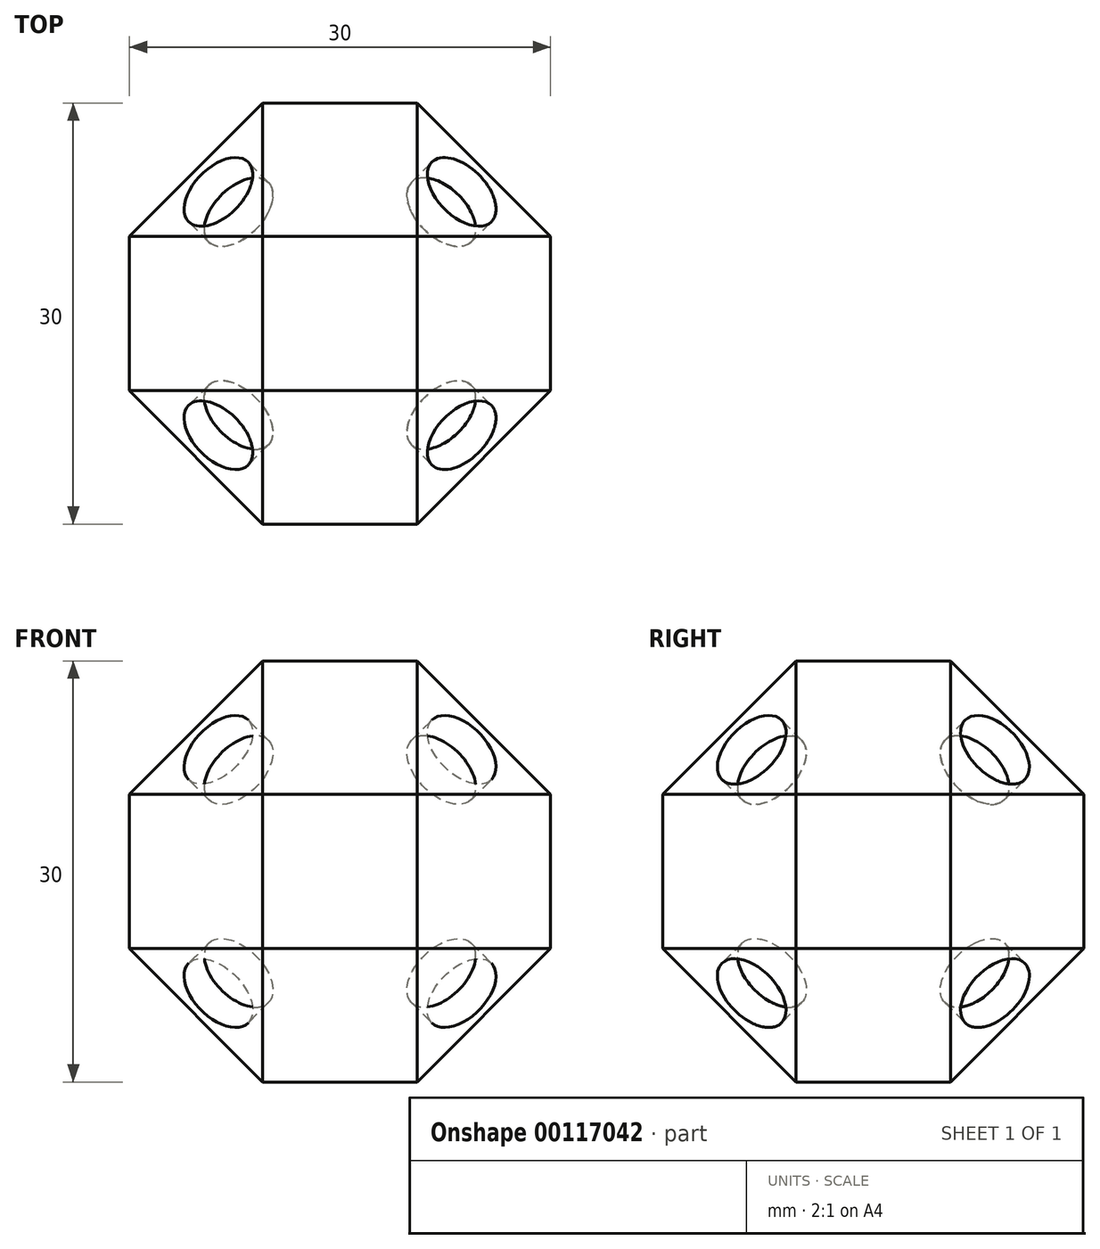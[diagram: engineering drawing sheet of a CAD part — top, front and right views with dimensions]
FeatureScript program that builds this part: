
annotation { "Feature Type Name" : "Feature", "Feature Type Description" : "" }
export const myFeature = defineFeature(function(context is Context, id is Id, definition is map)
    precondition{}
    {
        {
            var Q0;
            Q0=qCreatedBy(makeId("Front.planeOp"),FACE);
            var sketch = newSketch(context, id + "F0", { "sketchPlane" : qUnion([Q0])});
            skLineSegment(sketch, "E0.bottom", {"start": v(15, -15) * mm, "end": v(-15, -15) * mm});
            skLineSegment(sketch, "E0.top", {"start": v(15, 15) * mm, "end": v(-15, 15) * mm});
            skLineSegment(sketch, "E0.left", {"start": v(15, -15) * mm, "end": v(15, 15) * mm});
            skLineSegment(sketch, "E0.right", {"start": v(-15, -15) * mm, "end": v(-15, 15) * mm});
            skPoint(sketch, "E0.middle", {"position": v(0, 0) * mm});
            skLineSegment(sketch, "E1", {"start": v(15, 6.02) * mm, "end": v(6.02, 15) * mm, "construction": true});
            skLineSegment(sketch, "E2", {"start": v(15, 15) * mm, "end": v(10.5, 10.5) * mm, "construction": true});
            skSolve(sketch);
        }
        {
            var Q0;
            Q0 = qSketchRegion(id + "F0", true);
            extrude(context, id + "F1", {"entities" : qUnion([Q0]), "endBound" : BoundingType.SYMMETRIC, "depth" : 30 * mm});
        }
        {
            var Q0;
            Q0=makeQuery(id+"F1.opExtrude","CAP_EDGE",EDGE,{"disambiguationData":[OSD([sQuery(id+"F0.wireOp",EDGE,"E0.bottom")])],"isStart":true});
            var Q1;
            Q1=makeQuery(id+"F1.opExtrude","CAP_EDGE",EDGE,{"disambiguationData":[OSD([sQuery(id+"F0.wireOp",EDGE,"E0.top")])],"isStart":true});
            var Q2;
            Q2=makeQuery(id+"F1.opExtrude","CAP_EDGE",EDGE,{"disambiguationData":[OSD([sQuery(id+"F0.wireOp",EDGE,"E0.left")])],"isStart":true});
            var Q3;
            Q3=makeQuery(id+"F1.opExtrude","CAP_EDGE",EDGE,{"disambiguationData":[OSD([sQuery(id+"F0.wireOp",EDGE,"E0.right")])],"isStart":true});
            var Q4;
            Q4=makeQuery(id+"F1.opExtrude","SWEPT_EDGE",EDGE,{"disambiguationData":[OSD([sQuery(id+"F0.wireOp",EDGE,"E0.top"),sQuery(id+"F0.wireOp",EDGE,"E0.left")])]});
            var Q5;
            Q5=makeQuery(id+"F1.opExtrude","CAP_EDGE",EDGE,{"disambiguationData":[OSD([sQuery(id+"F0.wireOp",EDGE,"E0.top")])],"isStart":false});
            var Q6;
            Q6=makeQuery(id+"F1.opExtrude","SWEPT_EDGE",EDGE,{"disambiguationData":[OSD([sQuery(id+"F0.wireOp",EDGE,"E0.top"),sQuery(id+"F0.wireOp",EDGE,"E0.right")])]});
            var Q7;
            Q7=makeQuery(id+"F1.opExtrude","CAP_EDGE",EDGE,{"disambiguationData":[OSD([sQuery(id+"F0.wireOp",EDGE,"E0.right")])],"isStart":false});
            var Q8;
            Q8=makeQuery(id+"F1.opExtrude","CAP_EDGE",EDGE,{"disambiguationData":[OSD([sQuery(id+"F0.wireOp",EDGE,"E0.left")])],"isStart":false});
            var Q9;
            Q9=makeQuery(id+"F1.opExtrude","CAP_EDGE",EDGE,{"disambiguationData":[OSD([sQuery(id+"F0.wireOp",EDGE,"E0.bottom")])],"isStart":false});
            var Q10;
            Q10=makeQuery(id+"F1.opExtrude","SWEPT_EDGE",EDGE,{"disambiguationData":[OSD([sQuery(id+"F0.wireOp",EDGE,"E0.bottom"),sQuery(id+"F0.wireOp",EDGE,"E0.right")])]});
            var Q11;
            Q11=makeQuery(id+"F1.opExtrude","SWEPT_EDGE",EDGE,{"disambiguationData":[OSD([sQuery(id+"F0.wireOp",EDGE,"E0.bottom"),sQuery(id+"F0.wireOp",EDGE,"E0.left")])]});
            chamfer(context, id + "F2", {"entities" : qUnion([Q0, Q1, Q2, Q3, Q4, Q5, Q6, Q7, Q8, Q9, Q10, Q11]), "width" : 9.5 * mm, "tangentPropagation" : true});
        }
        {
            var Q0;
            {var subQ0=sQuery(id+"F0.wireOp",EDGE,"E0.left");var subQ1=sQuery(id+"F0.wireOp",EDGE,"E0.top");Q0=makeQuery(id+"F2.opChamfer","BLEND_FACE",FACE,{"disambiguationData":[OSD([subQ1,subQ0]),TDD([makeQuery(id+"F1.opExtrude","CAP_VERTEX",VERTEX,{"disambiguationData":[OSD([subQ1,subQ0])],"isStart":true})])]});}
            var sketch = newSketch(context, id + "F3", { "sketchPlane" : qUnion([Q0])});
            skCircle(sketch, "E3", {"center": v(0, 0) * mm, "radius": 3 * mm});
            skSolve(sketch);
        }
        {
            var Q0;
            Q0=makeQuery(id+"F3.imprint","IMPRINT",FACE,{"disambiguationData":[TD([[makeQuery(id+"F3.imprint","IMPRINT",EDGE,{"derivedFrom":sQuery(id+"F3.wireOp",EDGE,"E3")}),1.0]])]});
            extrude(context, id + "F4", {"entities" : qUnion([Q0]), "operationType" : NewBodyOperationType.REMOVE, "oppositeDirection" : true, "depth" : 2.5 * mm});
        }
        {
            var Q0;
            {var subQ0=sQuery(id+"F0.wireOp",EDGE,"E0.right");var subQ1=sQuery(id+"F0.wireOp",EDGE,"E0.top");Q0=makeQuery(id+"F2.opChamfer","BLEND_FACE",FACE,{"disambiguationData":[OSD([subQ1,subQ0]),TDD([makeQuery(id+"F1.opExtrude","CAP_VERTEX",VERTEX,{"disambiguationData":[OSD([subQ1,subQ0])],"isStart":true})])]});}
            var sketch = newSketch(context, id + "F5", { "sketchPlane" : qUnion([Q0])});
            skCircle(sketch, "E4", {"center": v(0, 0) * mm, "radius": 3 * mm});
            skSolve(sketch);
        }
        {
            var Q0;
            Q0=makeQuery(id+"F5.imprint","IMPRINT",FACE,{"disambiguationData":[TD([[makeQuery(id+"F5.imprint","IMPRINT",EDGE,{"derivedFrom":sQuery(id+"F5.wireOp",EDGE,"E4")}),1.0]])]});
            extrude(context, id + "F6", {"entities" : qUnion([Q0]), "operationType" : NewBodyOperationType.REMOVE, "oppositeDirection" : true, "depth" : 2.5 * mm});
        }
        {
            var Q0;
            {var subQ0=sQuery(id+"F0.wireOp",EDGE,"E0.right");var subQ1=sQuery(id+"F0.wireOp",EDGE,"E0.bottom");Q0=makeQuery(id+"F2.opChamfer","BLEND_FACE",FACE,{"disambiguationData":[OSD([subQ1,subQ0]),TDD([makeQuery(id+"F1.opExtrude","CAP_VERTEX",VERTEX,{"disambiguationData":[OSD([subQ1,subQ0])],"isStart":true})])]});}
            var sketch = newSketch(context, id + "F7", { "sketchPlane" : qUnion([Q0])});
            skCircle(sketch, "E5", {"center": v(0, 0) * mm, "radius": 3 * mm});
            skSolve(sketch);
        }
        {
            var Q0;
            Q0=makeQuery(id+"F7.imprint","IMPRINT",FACE,{"disambiguationData":[TD([[makeQuery(id+"F7.imprint","IMPRINT",EDGE,{"derivedFrom":sQuery(id+"F7.wireOp",EDGE,"E5")}),1.0]])]});
            extrude(context, id + "F8", {"entities" : qUnion([Q0]), "operationType" : NewBodyOperationType.REMOVE, "oppositeDirection" : true, "depth" : 2.5 * mm});
        }
        {
            var Q0;
            {var subQ0=sQuery(id+"F0.wireOp",EDGE,"E0.left");var subQ1=sQuery(id+"F0.wireOp",EDGE,"E0.bottom");Q0=makeQuery(id+"F2.opChamfer","BLEND_FACE",FACE,{"disambiguationData":[OSD([subQ1,subQ0]),TDD([makeQuery(id+"F1.opExtrude","CAP_VERTEX",VERTEX,{"disambiguationData":[OSD([subQ1,subQ0])],"isStart":true})])]});}
            var sketch = newSketch(context, id + "F9", { "sketchPlane" : qUnion([Q0])});
            skCircle(sketch, "E6", {"center": v(0, 0) * mm, "radius": 3 * mm});
            skSolve(sketch);
        }
        {
            var Q0;
            Q0=makeQuery(id+"F9.imprint","IMPRINT",FACE,{"disambiguationData":[TD([[makeQuery(id+"F9.imprint","IMPRINT",EDGE,{"derivedFrom":sQuery(id+"F9.wireOp",EDGE,"E6")}),1.0]])]});
            extrude(context, id + "F10", {"entities" : qUnion([Q0]), "operationType" : NewBodyOperationType.REMOVE, "oppositeDirection" : true, "depth" : 2.5 * mm});
        }
        {
            var Q0;
            {var subQ0=sQuery(id+"F0.wireOp",EDGE,"E0.right");var subQ1=sQuery(id+"F0.wireOp",EDGE,"E0.bottom");Q0=makeQuery(id+"F2.opChamfer","BLEND_FACE",FACE,{"disambiguationData":[OSD([subQ1,subQ0]),TDD([makeQuery(id+"F1.opExtrude","CAP_VERTEX",VERTEX,{"disambiguationData":[OSD([subQ1,subQ0])],"isStart":false})])]});}
            var sketch = newSketch(context, id + "F11", { "sketchPlane" : qUnion([Q0])});
            skCircle(sketch, "E7", {"center": v(0, 0) * mm, "radius": 3 * mm});
            skSolve(sketch);
        }
        {
            var Q0;
            Q0=makeQuery(id+"F11.imprint","IMPRINT",FACE,{"disambiguationData":[TD([[makeQuery(id+"F11.imprint","IMPRINT",EDGE,{"derivedFrom":sQuery(id+"F11.wireOp",EDGE,"E7")}),1.0]])]});
            extrude(context, id + "F12", {"entities" : qUnion([Q0]), "operationType" : NewBodyOperationType.REMOVE, "oppositeDirection" : true, "depth" : 2.5 * mm});
        }
        {
            var Q0;
            {var subQ0=sQuery(id+"F0.wireOp",EDGE,"E0.right");var subQ1=sQuery(id+"F0.wireOp",EDGE,"E0.top");Q0=makeQuery(id+"F2.opChamfer","BLEND_FACE",FACE,{"disambiguationData":[OSD([subQ1,subQ0]),TDD([makeQuery(id+"F1.opExtrude","CAP_VERTEX",VERTEX,{"disambiguationData":[OSD([subQ1,subQ0])],"isStart":false})])]});}
            var sketch = newSketch(context, id + "F13", { "sketchPlane" : qUnion([Q0])});
            skCircle(sketch, "E8", {"center": v(0, 0) * mm, "radius": 3 * mm});
            skSolve(sketch);
        }
        {
            var Q0;
            Q0=makeQuery(id+"F13.imprint","IMPRINT",FACE,{"disambiguationData":[TD([[makeQuery(id+"F13.imprint","IMPRINT",EDGE,{"derivedFrom":sQuery(id+"F13.wireOp",EDGE,"E8")}),1.0]])]});
            extrude(context, id + "F14", {"entities" : qUnion([Q0]), "operationType" : NewBodyOperationType.REMOVE, "oppositeDirection" : true, "depth" : 2.5 * mm});
        }
        {
            var Q0;
            {var subQ0=sQuery(id+"F0.wireOp",EDGE,"E0.left");var subQ1=sQuery(id+"F0.wireOp",EDGE,"E0.top");Q0=makeQuery(id+"F2.opChamfer","BLEND_FACE",FACE,{"disambiguationData":[OSD([subQ1,subQ0]),TDD([makeQuery(id+"F1.opExtrude","CAP_VERTEX",VERTEX,{"disambiguationData":[OSD([subQ1,subQ0])],"isStart":false})])]});}
            var sketch = newSketch(context, id + "F15", { "sketchPlane" : qUnion([Q0])});
            skCircle(sketch, "E9", {"center": v(0, 0) * mm, "radius": 3 * mm});
            skSolve(sketch);
        }
        {
            var Q0;
            Q0=makeQuery(id+"F15.imprint","IMPRINT",FACE,{"disambiguationData":[TD([[makeQuery(id+"F15.imprint","IMPRINT",EDGE,{"derivedFrom":sQuery(id+"F15.wireOp",EDGE,"E9")}),1.0]])]});
            extrude(context, id + "F16", {"entities" : qUnion([Q0]), "operationType" : NewBodyOperationType.REMOVE, "oppositeDirection" : true, "depth" : 2.5 * mm});
        }
        {
            var Q0;
            {var subQ0=sQuery(id+"F0.wireOp",EDGE,"E0.left");var subQ1=sQuery(id+"F0.wireOp",EDGE,"E0.bottom");Q0=makeQuery(id+"F2.opChamfer","BLEND_FACE",FACE,{"disambiguationData":[OSD([subQ1,subQ0]),TDD([makeQuery(id+"F1.opExtrude","CAP_VERTEX",VERTEX,{"disambiguationData":[OSD([subQ1,subQ0])],"isStart":false})])]});}
            var sketch = newSketch(context, id + "F17", { "sketchPlane" : qUnion([Q0])});
            skCircle(sketch, "E10", {"center": v(0, 0) * mm, "radius": 3 * mm});
            skLineSegment(sketch, "E11", {"start": v(0, 0) * mm, "end": v(3.88, 0) * mm, "construction": true});
            skPoint(sketch, "E12", {"position": v(3, 0) * mm});
            skSolve(sketch);
        }
        {
            var Q0;
            Q0=makeQuery(id+"F17.imprint","IMPRINT",FACE,{"disambiguationData":[TD([[makeQuery(id+"F17.imprint","IMPRINT",EDGE,{"derivedFrom":sQuery(id+"F17.wireOp",EDGE,"E10")}),1.0]])]});
            extrude(context, id + "F18", {"entities" : qUnion([Q0]), "operationType" : NewBodyOperationType.REMOVE, "oppositeDirection" : true, "depth" : 2.5 * mm});
        }
    });
